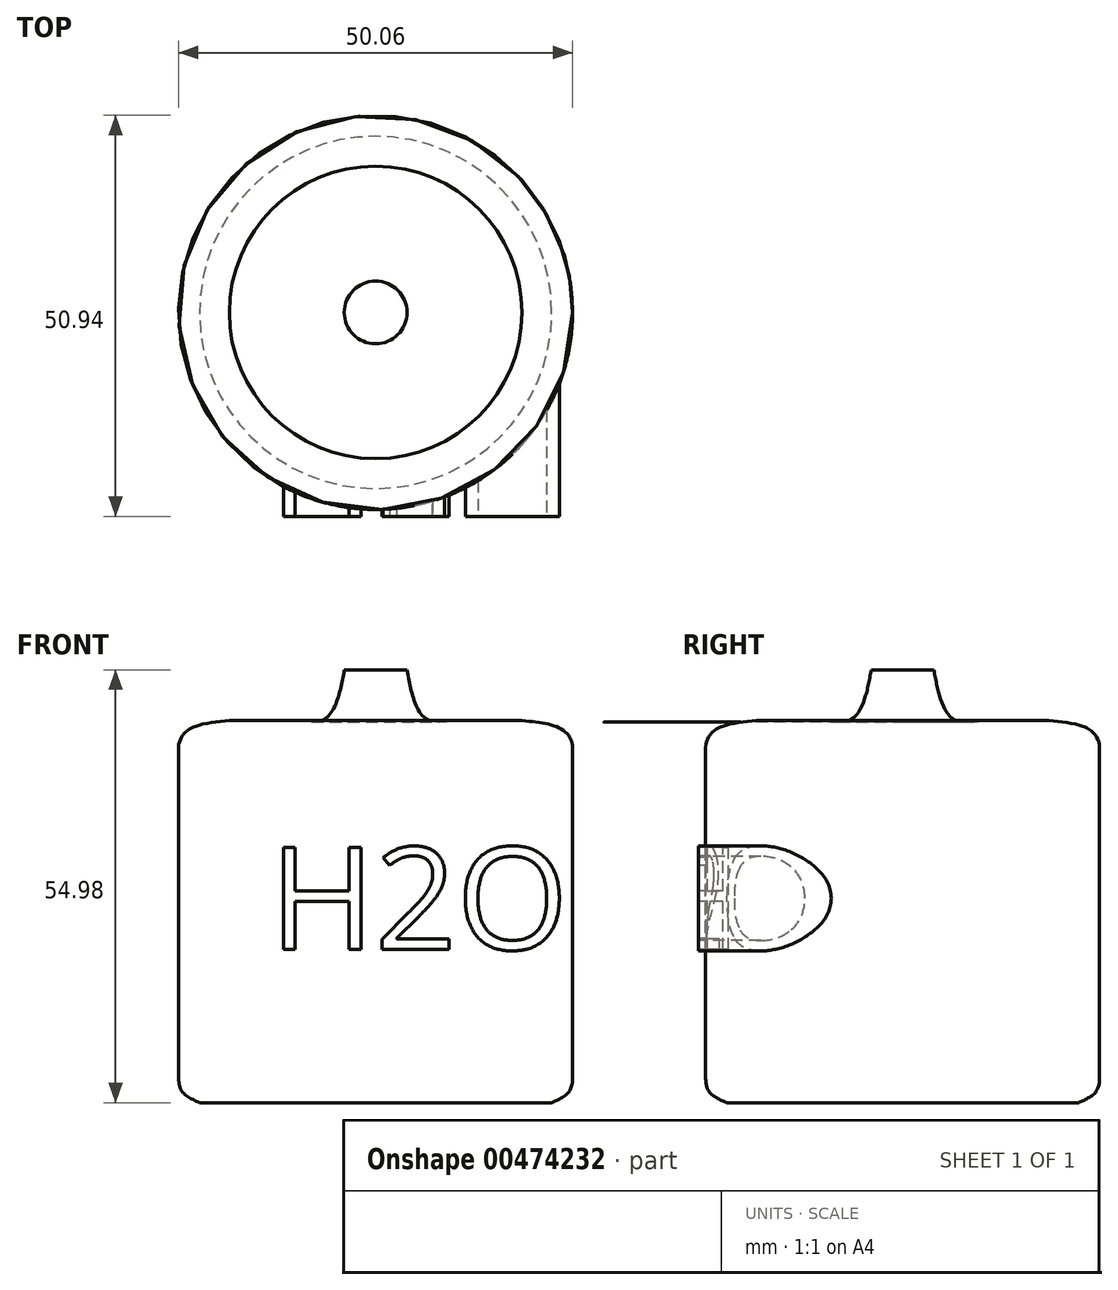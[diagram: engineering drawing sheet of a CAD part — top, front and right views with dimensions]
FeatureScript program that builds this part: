
annotation { "Feature Type Name" : "Feature", "Feature Type Description" : "" }
export const myFeature = defineFeature(function(context is Context, id is Id, definition is map)
    precondition{}
    {
        {
            var Q0;
            Q0=qCreatedBy(makeId("Front.planeOp"),FACE);
            var sketch = newSketch(context, id + "F0", { "sketchPlane" : qUnion([Q0])});
            skLineSegment(sketch, "E0", {"start": v(0, 0) * mm, "end": v(-22.37, 0) * mm});
            skFitSpline(sketch, "E1", {"points": [v(-22.37, 0) * mm, v(-24.65, 1.52) * mm, v(-25.03, 3.98) * mm], "startDerivative": vector(-5.39, 2.43) * mm, "endDerivative": vector(0, 5.56) * mm});
            skLineSegment(sketch, "E2", {"start": v(-25.03, 3.98) * mm, "end": v(-25.03, 45.12) * mm});
            skFitSpline(sketch, "E3", {"points": [v(-25.03, 45.12) * mm, v(-23.7, 47.4) * mm, v(-18.58, 48.54) * mm], "startDerivative": vector(0, 6.55) * mm, "endDerivative": vector(10.37, 0.9) * mm});
            skLineSegment(sketch, "E4", {"start": v(-18.58, 48.54) * mm, "end": v(-11.38, 48.54) * mm});
            skFitSpline(sketch, "E5", {"points": [v(-11.38, 48.54) * mm, v(-6.83, 48.54) * mm, v(-4.93, 51) * mm, v(-3.98, 54.98) * mm], "startDerivative": vector(14.36, 0) * mm, "endDerivative": vector(2.16, 12.07) * mm});
            skLineSegment(sketch, "E6", {"start": v(-3.98, 54.98) * mm, "end": v(0, 54.98) * mm});
            skLineSegment(sketch, "E7", {"start": v(0, 54.98) * mm, "end": v(0, 0) * mm});
            skSolve(sketch);
        }
        {
            var Q0;
            Q0 = qSketchRegion(id + "F0", true);
            var Q1;
            Q1=sQuery(id+"F0.wireOp",EDGE,"E7");
            revolve(context, id + "F1", {"entities" : qUnion([Q0]), "axis" : qUnion([Q1]), "revolveType" : RevolveType.FULL});
        }
        {
            var Q0;
            Q0=qCreatedBy(makeId("Front.planeOp"),FACE);
            cPlane(context, id + "F2", {"entities" : qUnion([Q0]), "cplaneType" : CPlaneType.OFFSET, "offset" : 25.9 * mm, "width" : 152.4 * mm, "height" : 152.4 * mm});
        }
        {
            var Q0;
            Q0=qCreatedBy(id+"F2.planeOp",FACE);
            var sketch = newSketch(context, id + "F3", { "sketchPlane" : qUnion([Q0])});
            skText(sketch, "E8", { "text": "H2O", "fontName": "OpenSans-Regular.ttf"});
            const initialGuessF3  = {"E8": [-0.0135, 0.01946, 1, 0, 0.01308]};
            skSetInitialGuess(sketch, initialGuessF3);
            skSolve(sketch);
        }
        {
            var Q0;
            Q0 = qSketchRegion(id + "F3", true);
            var Q1;
            Q1=makeQuery(id+"F1.opRevolve","SWEPT_FACE",FACE,{"disambiguationData":[OSD([sQuery(id+"F0.wireOp",EDGE,"E2")])]});
            extrude(context, id + "F4", {"entities" : qUnion([Q0]), "operationType" : NewBodyOperationType.ADD, "endBound" : BoundingType.UP_TO_SURFACE, "oppositeDirection" : true, "endBoundEntityFace" : qUnion([Q1]), "depth" : 25.4 * mm});
        }
    });
